# Revit family: Diverter-GROHE-Allure_Brilliant-19799000
name_source: partatom
category: Plumbing Fixtures
revit_build: Autodesk Revit 2014 (Build: 20130308_1515(x64)
units: mm (PartAtom-declared; Revit-internal decimal feet)

## types (1)
- 19799000
    Assembly Code = D2010710
    CW Connection = Yes
    CWFU = 3
    Cold Water Connection Diameter = 1/2"
    Cold Water Connection Radius = 1/4"
    Default Elevation = 44"
    Description = Allure Brilliant 5-Port Diverter Trim
    Finish = Metal-Grohe-000-Chrome
    Flow Rate = 14 gpm at 45 psi
    HW Connection = Yes
    HWFU = 3
    Height = 40"
    Hot Water Connection Diameter = 1"
    Hot Water Connection Radius = 1/4"
    Installation Type = Wall Mounted
    Length = 3 7/16"
    Manufacturer = Grohe
    Material = Metal-Grohe-000-Chrome
    Model = 19799000
    Price = Prices may vary. Please consult Manufacturer Representative for most up-to-date price list.
    Product Page URL = https://www.grohe.us
    Shipping Weight = 0.838 lb
    Tempered Connection Diameter = 1/2"
    Tempered Connection Radius = 1/4"
    URL = https://www.grohe.us
    Vent Connection = No
    WFU = 4
    Warranty Documentation Link = https://cdn.cloud.grohe.com
    Waste Connection = No
    Width = 6 11/16"

## geometry (parser evidence)
native form markers: Sweep x3
no freeform markers — native parametric forms only
